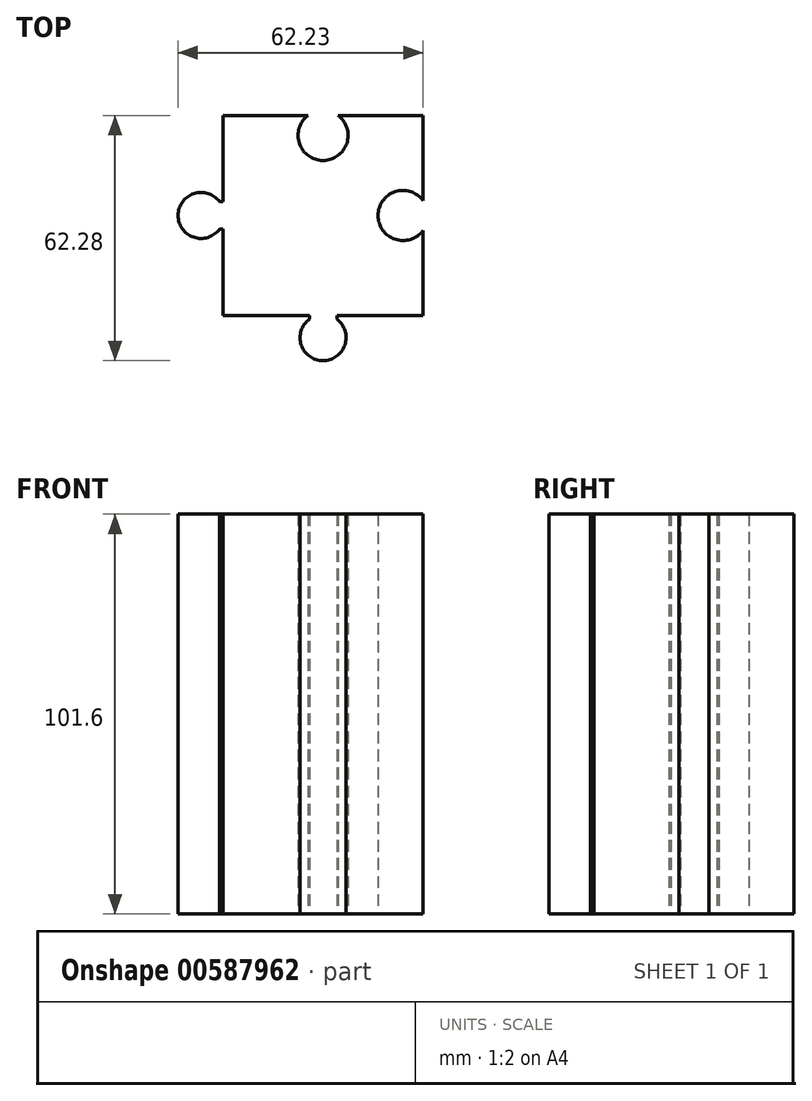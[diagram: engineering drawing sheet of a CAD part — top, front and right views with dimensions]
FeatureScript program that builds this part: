
annotation { "Feature Type Name" : "Feature", "Feature Type Description" : "" }
export const myFeature = defineFeature(function(context is Context, id is Id, definition is map)
    precondition{}
    {
        {
            var Q0;
            Q0=qCreatedBy(makeId("Top.planeOp"),FACE);
            var sketch = newSketch(context, id + "F0", { "sketchPlane" : qUnion([Q0])});
            skLineSegment(sketch, "E0.bottom", {"start": v(0, 0) * mm, "end": v(21.9, 0) * mm});
            skLineSegment(sketch, "E0.top", {"start": v(0, 50.8) * mm, "end": v(21.59, 50.8) * mm});
            skLineSegment(sketch, "E0.left", {"start": v(0, 0) * mm, "end": v(0, 21.9) * mm});
            skLineSegment(sketch, "E0.right", {"start": v(50.8, 0) * mm, "end": v(50.8, 21.6) * mm});
            skArc(sketch, "E1", {"start": v(21.59, 50.8) * mm, "mid": v(25.4, 39.37) * mm, "end": v(29.2, 50.8) * mm});
            skArc(sketch, "E2", {"start": v(50.8, 29.2) * mm, "mid": v(39.37, 25.4) * mm, "end": v(50.8, 21.6) * mm});
            skLineSegment(sketch, "E3.trimOffspring", {"start": v(29.2, 50.8) * mm, "end": v(50.8, 50.8) * mm});
            skLineSegment(sketch, "E4.trimOffspring", {"start": v(50.8, 29.2) * mm, "end": v(50.8, 50.8) * mm});
            skArc(sketch, "E5.0", {"start": v(21.9, -0.96) * mm, "mid": v(25.4, -11.48) * mm, "end": v(28.9, -0.96) * mm});
            skArc(sketch, "E6.0", {"start": v(-0.91, 28.9) * mm, "mid": v(-11.43, 25.4) * mm, "end": v(-0.91, 21.9) * mm});
            skLineSegment(sketch, "E7", {"start": v(21.9, -0.96) * mm, "end": v(21.9, 0) * mm});
            skLineSegment(sketch, "E8", {"start": v(28.9, -0.96) * mm, "end": v(28.9, 0) * mm});
            skLineSegment(sketch, "E9", {"start": v(-0.91, 21.9) * mm, "end": v(0, 21.9) * mm});
            skLineSegment(sketch, "E10", {"start": v(0, 28.9) * mm, "end": v(-0.91, 28.9) * mm});
            skLineSegment(sketch, "E11.trimOffspring", {"start": v(0, 28.9) * mm, "end": v(0, 50.8) * mm});
            skLineSegment(sketch, "E12.trimOffspring", {"start": v(28.9, 0) * mm, "end": v(50.8, 0) * mm});
            skSolve(sketch);
        }
        {
            var Q0;
            Q0=makeQuery(id+"F0.imprint","IMPRINT",FACE,{"disambiguationData":[TD([[makeQuery(id+"F0.imprint","IMPRINT",EDGE,{"derivedFrom":sQuery(id+"F0.wireOp",EDGE,"E0.bottom")}),1.0]])]});
            extrude(context, id + "F1", {"entities" : qUnion([Q0]), "depth" : 101.6 * mm, "offsetDistance" : 25.4 * mm});
        }
    });
